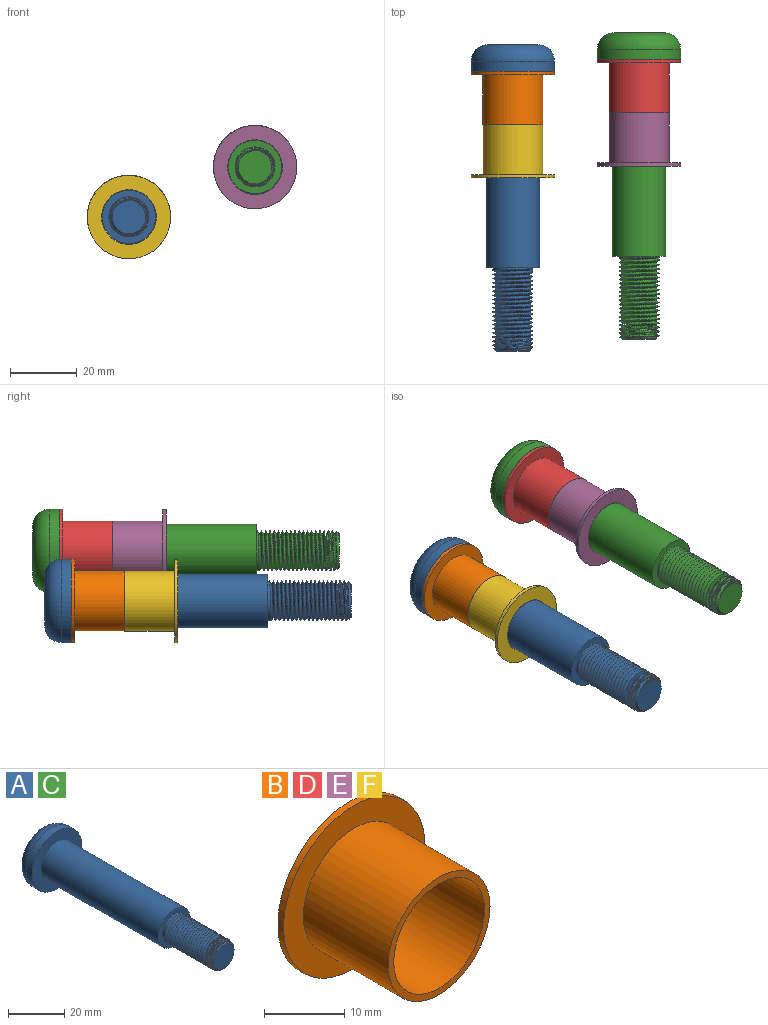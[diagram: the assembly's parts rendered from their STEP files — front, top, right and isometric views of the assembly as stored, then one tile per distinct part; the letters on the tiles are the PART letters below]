
ASSEMBLY  parts=6 mates=4
PART A: 38 faces, bbox 27.1x92.7x27.1 mm
  f0: plane 15x15mm, normal (0,1,0), area 90.1mm2, adj f3,f31,f32,f33,f34,f35,f36
  f1: cylinder r=12.5mm len=25mm, axis (0,1,0), area 235.6mm2, adj f2,f3
  f2: plane 25x25mm, normal (0,-1,0), area 289.8mm2, adj f1,f4
  f3: torus R=7.5mm, axis (0,-1,0), area 527.2mm2, adj f0,f1
  f4: cylinder r=8mm len=59mm, axis (0,1,0), area 2965.7mm2, adj f2,f5
  f5: plane 16x16mm, normal (0,-1,0), area 88mm2, adj f4,f25
  f6: cylinder r=6mm len=4.44mm, axis (0,1,0), area 0.3mm2, adj f7,f27,f29,f30
  f7: cylinder r=6mm len=12mm, axis (0,1,0), area 2.6mm2, adj f6,f8,f29,f30
  f8: cylinder r=6mm len=12mm, axis (0,1,0), area 2.6mm2, adj f7,f9,f29,f30
  f9: cylinder r=6mm len=12mm, axis (0,1,0), area 2.7mm2, adj f8,f10,f29,f30
  f10: cylinder r=6mm len=12mm, axis (0,1,0), area 2.6mm2, adj f9,f11,f29,f30
  f11: cylinder r=6mm len=12mm, axis (0,1,0), area 2.7mm2, adj f10,f12,f29,f30
  f12: cylinder r=6mm len=12mm, axis (0,1,0), area 2.6mm2, adj f11,f13,f29,f30
  f13: cylinder r=6mm len=12mm, axis (0,1,0), area 2.6mm2, adj f12,f14,f29,f30
  f14: cylinder r=6mm len=12mm, axis (0,1,0), area 2.6mm2, adj f13,f15,f29,f30
  f15: cylinder r=6mm len=12mm, axis (0,1,0), area 2.7mm2, adj f14,f16,f29,f30
  f16: cylinder r=6mm len=12mm, axis (0,1,0), area 2.7mm2, adj f15,f17,f29,f30
  f17: cylinder r=6mm len=12mm, axis (0,1,0), area 2.6mm2, adj f16,f18,f29,f30
  f18: cylinder r=6mm len=12mm, axis (0,1,0), area 2.6mm2, adj f17,f19,f29,f30
  f19: cylinder r=6mm len=12mm, axis (0,1,0), area 2.6mm2, adj f18,f20,f29,f30
  f20: cylinder r=6mm len=12mm, axis (0,1,0), area 2.7mm2, adj f19,f21,f29,f30
  f21: cylinder r=6mm len=12mm, axis (0,1,0), area 2.6mm2, adj f20,f22,f29,f30
  f22: cylinder r=6mm len=12mm, axis (0,1,0), area 2.6mm2, adj f21,f23,f29,f30
  f23: cylinder r=6mm len=12mm, axis (0,1,0), area 2.6mm2, adj f22,f24,f29,f30
  f24: cylinder r=6mm len=12mm, axis (0,1,0), area 2.6mm2, adj f23,f25,f29,f30
  f25: cylinder r=6mm len=12mm, axis (0,1,0), area 29.3mm2, adj f5,f24,f28,f30
  f26: plane 10x10mm, normal (0,-1,0), area 78.5mm2, adj f27,f29,f30
  f27: cone r=5mm half-angle=45deg, axis (0,1,0), area 24.6mm2, adj f6,f26,f29,f30
  f28: plane 1.18x1.02mm, normal (0,0,-1), area 0.6mm2, adj f25,f29,f30
  f29: bspline ~24.97x13.86mm, area 764.4mm2, adj f6,f7,f8,f9,f10,f11,f12,f13
  f30: bspline ~24.97x13.86mm, area 783.6mm2, adj f6,f7,f8,f9,f10,f11,f12,f13
  f31: plane 5x5mm, normal (0.87,0,0.5), area 28.9mm2, adj f0,f32,f36,f37
  f32: plane 5x5mm, normal (0.87,0,-0.5), area 28.9mm2, adj f0,f31,f33,f37
  f33: plane 5.77x5mm, normal (0,0,-1), area 28.9mm2, adj f0,f32,f34,f37
  f34: plane 5x5mm, normal (-0.87,0,-0.5), area 28.9mm2, adj f0,f33,f35,f37
  f35: plane 5x5mm, normal (-0.87,0,0.5), area 28.9mm2, adj f0,f34,f36,f37
  f36: plane 5.77x5mm, normal (0,0,1), area 28.9mm2, adj f0,f31,f35,f37
  f37: plane 11.55x10mm, normal (0,1,0), area 86.6mm2, adj f31,f32,f33,f34,f35,f36
PART B: 7 faces, bbox 25x16x25 mm
  f0: cylinder r=12.5mm len=25mm, axis (0,1,0), area 78.5mm2, adj f1,f2
  f1: plane 25x25mm, normal (0,-1,0), area 236.4mm2, adj f0,f4
  f2: plane 25x25mm, normal (0,1,0), area 279.6mm2, adj f0,f6
  f3: cylinder r=8mm len=16mm, axis (0,1,0), area 794.2mm2, adj f5,f6
  f4: cylinder r=9mm len=18mm, axis (0,1,0), area 848.2mm2, adj f1,f5
  f5: plane 18x18mm, normal (0,-1,0), area 53.4mm2, adj f3,f4
  f6: torus R=8.2mm, axis (0,-1,0), area 15.9mm2, adj f2,f3
PART C: same geometry as A
PART D: same geometry as B
PART E: same geometry as B
PART F: same geometry as B
PLACE A rot(axis=(0,1,0),180deg) t=(-13.41,37.18,-13.62)mm
PLACE B rot(axis=(0,1,0),90deg) t=(-13.41,29.18,-13.62)mm
PLACE C rot(axis=(0,1,0),180deg) t=(24.43,40.7,1.36)mm
PLACE D rot(axis=(0,1,0),90deg) t=(24.43,32.7,1.36)mm
PLACE E rot(axis=(1,0,0),180deg) t=(24.45,0.71,1.31)mm
PLACE F rot(axis=(1,0,0),180deg) t=(-13.39,-2.82,-13.67)mm
MATE parallel F.f0 <-> A.f1  axis (0,1,0) through (-13.39,13.18,-13.67)mm
MATE parallel A.f1 <-> B.f0  axis (0,-1,0) through (-13.41,29.18,-13.62)mm
MATE parallel C.f1 <-> D.f0  axis (0,-1,0) through (24.43,32.7,1.36)mm
MATE parallel E.f0 <-> C.f1  axis (0,1,0) through (24.45,16.71,1.31)mm
